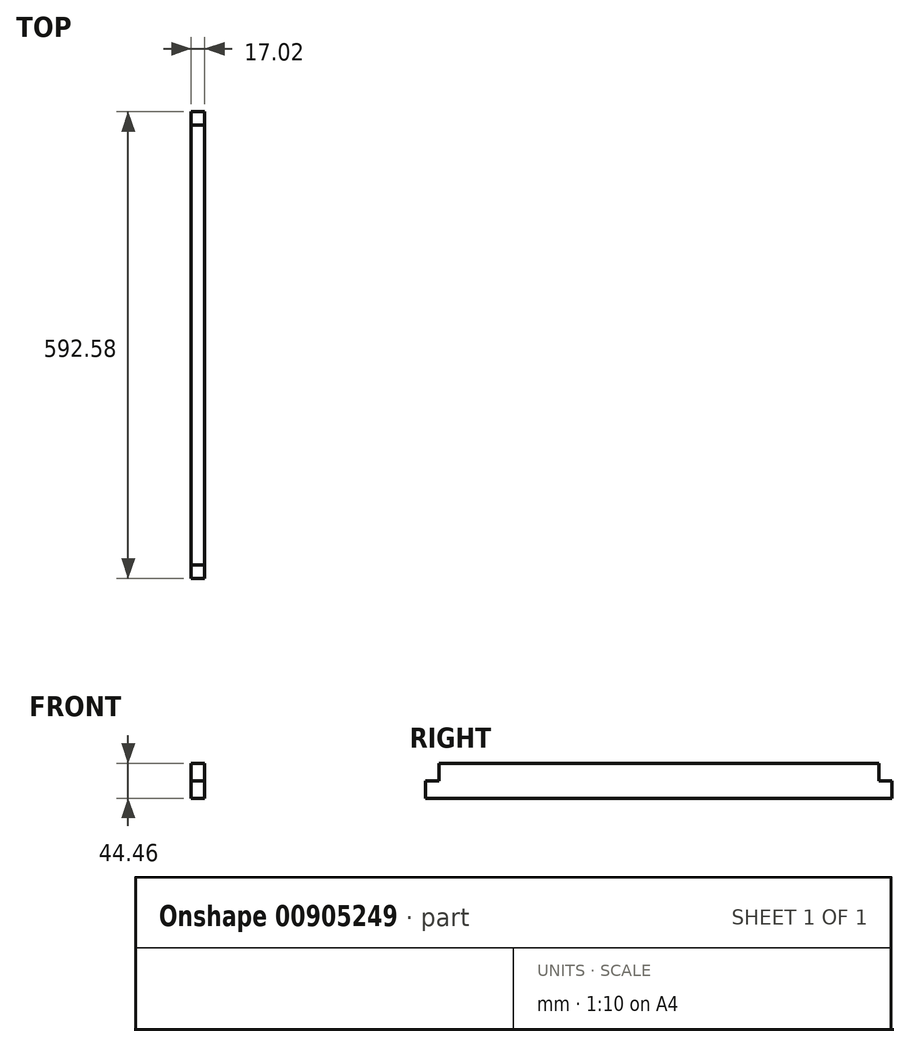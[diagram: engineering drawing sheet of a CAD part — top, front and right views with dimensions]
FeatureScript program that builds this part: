
annotation { "Feature Type Name" : "Feature", "Feature Type Description" : "" }
export const myFeature = defineFeature(function(context is Context, id is Id, definition is map)
    precondition{}
    {
        {
            var Q0;
            Q0=qCreatedBy(makeId("Right.planeOp"),FACE);
            var sketch = newSketch(context, id + "F0", { "sketchPlane" : qUnion([Q0])});
            skLineSegment(sketch, "E0.bottom", {"start": v(296.3, -22.23) * mm, "end": v(-296.3, -22.23) * mm});
            skLineSegment(sketch, "E0.top", {"start": v(296.3, 22.23) * mm, "end": v(-296.3, 22.22) * mm});
            skLineSegment(sketch, "E0.left", {"start": v(296.3, -22.23) * mm, "end": v(296.3, 22.22) * mm});
            skLineSegment(sketch, "E0.right", {"start": v(-296.3, -22.23) * mm, "end": v(-296.3, 22.22) * mm});
            skPoint(sketch, "E0.middle", {"position": v(0, 0) * mm});
            skSolve(sketch);
        }
        {
            var Q0;
            Q0=qSketchRegion(id+"F0",true);
            extrude(context, id + "F1", {"entities" : qUnion([Q0]), "offsetDistance" : 25.4 * mm, "depth" : 17.02 * mm});
        }
        {
            var Q0;
            Q0=makeQuery(id+"F1.opExtrude","CAP_FACE",FACE,{"disambiguationData":[OSD([sQuery(id+"F0.wireOp",EDGE,"E0.bottom"),sQuery(id+"F0.wireOp",EDGE,"E0.top"),sQuery(id+"F0.wireOp",EDGE,"E0.left"),sQuery(id+"F0.wireOp",EDGE,"E0.right")])],"isStart":false});
            var sketch = newSketch(context, id + "F2", { "sketchPlane" : qUnion([Q0])});
            skLineSegment(sketch, "E1.bottom", {"start": v(-296.3, 22.22) * mm, "end": v(-279.27, 22.22) * mm});
            skLineSegment(sketch, "E1.top", {"start": v(-296.3, 0) * mm, "end": v(-279.27, 0) * mm});
            skLineSegment(sketch, "E1.left", {"start": v(-296.3, 22.22) * mm, "end": v(-296.3, 0) * mm});
            skLineSegment(sketch, "E1.right", {"start": v(-279.27, 22.22) * mm, "end": v(-279.27, 0) * mm});
            skLineSegment(sketch, "E2.MirrorCS", {"start": v(279.27, 22.22) * mm, "end": v(279.27, 0) * mm});
            skLineSegment(sketch, "E3.MirrorCS", {"start": v(296.3, 22.22) * mm, "end": v(296.3, 0) * mm});
            skLineSegment(sketch, "E4.MirrorCS", {"start": v(296.3, 22.22) * mm, "end": v(279.27, 22.22) * mm});
            skLineSegment(sketch, "E5.MirrorCS", {"start": v(296.3, 0) * mm, "end": v(279.27, 0) * mm});
            skSolve(sketch);
        }
        {
            var Q0;
            Q0=qSketchRegion(id+"F2",true);
            extrude(context, id + "F3", {"entities" : qUnion([Q0]), "operationType" : NewBodyOperationType.REMOVE, "endBound" : BoundingType.THROUGH_ALL, "oppositeDirection" : true, "depth" : 25.4 * mm});
        }
    });
